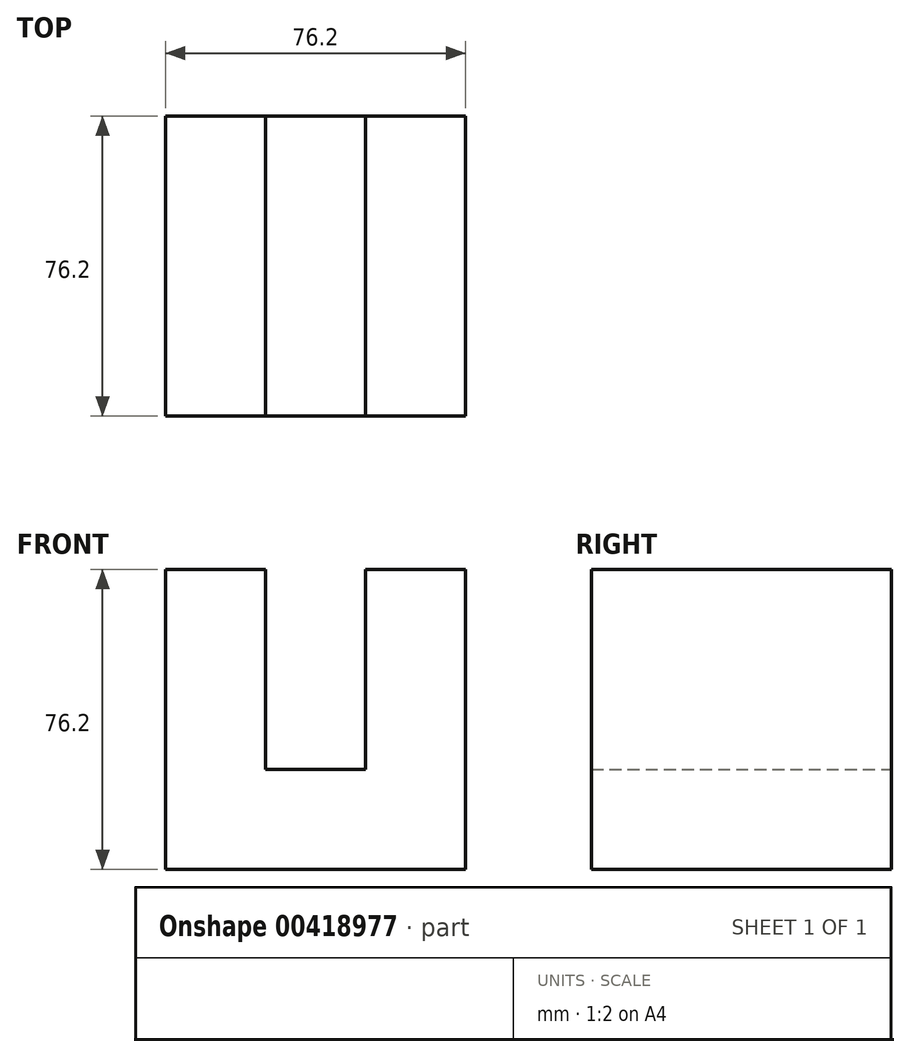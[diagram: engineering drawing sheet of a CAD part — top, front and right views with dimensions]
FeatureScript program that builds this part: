
annotation { "Feature Type Name" : "Feature", "Feature Type Description" : "" }
export const myFeature = defineFeature(function(context is Context, id is Id, definition is map)
    precondition{}
    {
        {
            var Q0;
            Q0=qCreatedBy(makeId("Front.planeOp"),FACE);
            var sketch = newSketch(context, id + "F0", { "sketchPlane" : qUnion([Q0])});
            skLineSegment(sketch, "E0", {"start": v(0, 0) * mm, "end": v(-76.2, 0) * mm});
            skLineSegment(sketch, "E1", {"start": v(-76.2, 0) * mm, "end": v(-76.2, 76.2) * mm});
            skLineSegment(sketch, "E2", {"start": v(-76.2, 76.2) * mm, "end": v(-50.8, 76.2) * mm});
            skLineSegment(sketch, "E3", {"start": v(-50.8, 76.2) * mm, "end": v(-50.8, 25.4) * mm});
            skLineSegment(sketch, "E4", {"start": v(-50.8, 25.4) * mm, "end": v(-25.4, 25.4) * mm});
            skLineSegment(sketch, "E5", {"start": v(-25.4, 25.4) * mm, "end": v(-25.4, 76.2) * mm});
            skLineSegment(sketch, "E6", {"start": v(-25.4, 76.2) * mm, "end": v(0, 76.2) * mm});
            skLineSegment(sketch, "E7", {"start": v(0, 76.2) * mm, "end": v(0, 0) * mm});
            skSolve(sketch);
        }
        {
            var Q0;
            Q0=makeQuery(id+"F0.imprint","IMPRINT",FACE,{"disambiguationData":[TD([[makeQuery(id+"F0.imprint","IMPRINT",EDGE,{"derivedFrom":sQuery(id+"F0.wireOp",EDGE,"E0")}),-1.0]])]});
            extrude(context, id + "F1", {"entities" : qUnion([Q0]), "depth" : 76.2 * mm});
        }
    });
